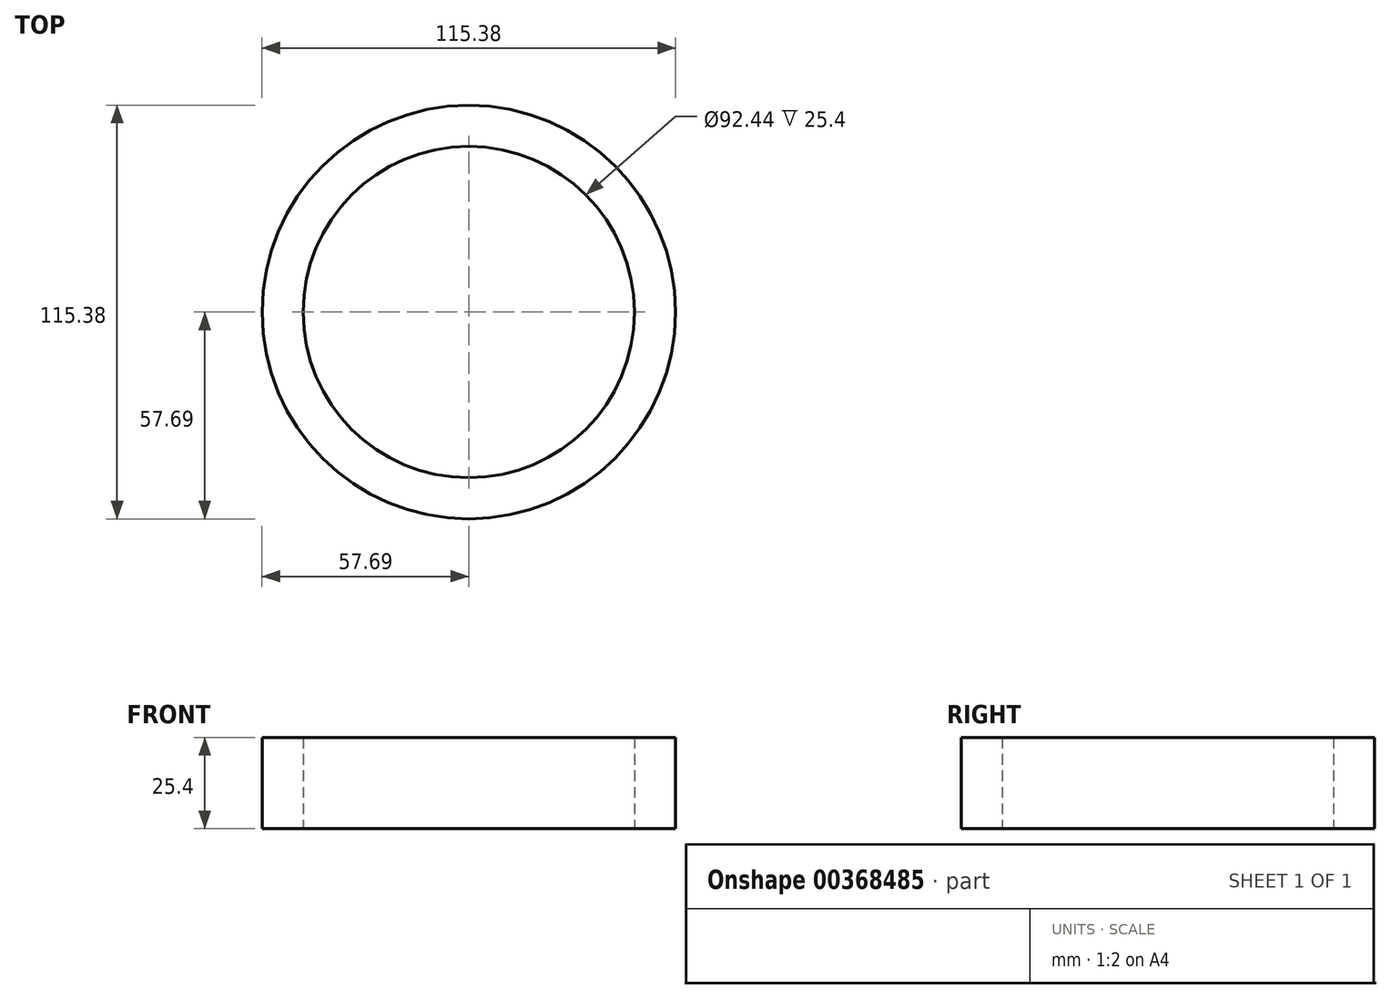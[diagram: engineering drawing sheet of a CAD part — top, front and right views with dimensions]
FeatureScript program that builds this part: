
annotation { "Feature Type Name" : "Feature", "Feature Type Description" : "" }
export const myFeature = defineFeature(function(context is Context, id is Id, definition is map)
    precondition{}
    {
        {
            var Q0;
            Q0=qCreatedBy(makeId("Top.planeOp"),FACE);
            var sketch = newSketch(context, id + "F0", { "sketchPlane" : qUnion([Q0])});
            skCircle(sketch, "E0", {"center": v(0, 0) * mm, "radius": 57.69 * mm});
            skCircle(sketch, "E1", {"center": v(0, 0) * mm, "radius": 46.22 * mm});
            skSolve(sketch);
        }
        {
            var Q0;
            Q0=makeQuery(id+"F0.imprint","IMPRINT",FACE,{"disambiguationData":[TD([[makeQuery(id+"F0.imprint","IMPRINT",EDGE,{"derivedFrom":sQuery(id+"F0.wireOp",EDGE,"E0")}),1.0]])]});
            extrude(context, id + "F1", {"entities" : qUnion([Q0]), "depth" : 25.4 * mm});
        }
    });
